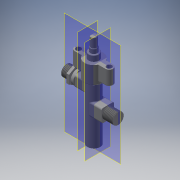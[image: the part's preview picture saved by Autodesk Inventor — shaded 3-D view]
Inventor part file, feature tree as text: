
AUTODESK INVENTOR PART (.ipt)
format: ipt  version: 2018 (Build 220112000, 112)  size: 577,024 bytes
history: native  units: mm
features: extrude x15, sketch x15, fillet x6, projected_geometry x5, hole x3, plane x3, thread x2
ambient origin geometry x8: Origin, YZ Plane, XZ Plane, XY Plane, X Axis, Y Axis, Z Axis, Center Point
bodies: Volumenkörper1 (feature_tree)
feature tree (49):
  extrude  "Extrusion1"  Depth=18.0mm
  extrude  "Extrusion2"  Depth=10.675mm
  extrude  "Extrusion3"  Depth=17.0mm TaperAngle=0.0deg
  extrude  "Extrusion4"  Depth=6.5mm TaperAngle=0.0deg
  hole  "Bohrung1"  [1 undecoded]
  hole  "Bohrung2"  [1 undecoded]
  extrude  "Extrusion5"  Depth=10.0mm
  extrude  "Extrusion6"  Depth=10.0mm
  plane  "Arbeitsebene1"
  extrude  "Extrusion7"  Depth=8.0mm TaperAngle=0.0deg
  extrude  "Extrusion8"  Depth=66.0mm TaperAngle=0.0deg
  thread  "Gewinde1"  [1 undecoded]
  extrude  "Extrusion9"  Depth=19.0mm
  plane  "Arbeitsebene2"
  extrude  "Extrusion10"  Depth=13.0mm
  extrude  "Extrusion11"  Depth=10.0mm TaperAngle=0.0deg
  fillet  "Rundung1"  Radius=6.0mm
  fillet  "Rundung2"  Radius=13.0mm
  extrude  "Extrusion12"  Depth=5.0mm
  fillet  "Rundung3"  Radius=8.8mm
  fillet  "Rundung4"  Radius=16.0mm
  fillet  "Rundung5"  Radius=3.0mm
  fillet  "Rundung6"  Radius=2.0mm
  extrude  "Extrusion13"  Depth=6.0mm TaperAngle=0.0deg
  extrude  "Extrusion14"  Depth=8.0mm
  extrude  "Extrusion15"  Depth=8.0mm
  thread  "Gewinde2"  [1 undecoded]
  hole  "Bohrung4"  [1 undecoded]
  plane  "Arbeitsebene3"
  sketch  "Skizze1"  dims[d0=21.35mm d1=18.0mm]
  sketch  "Skizze2"  dims[d2=9.0mm d3=10.675mm]
  sketch  "Skizze3"  dims[d4=10.675mm d5=17.0mm d6=0.0mm]
  sketch  "Skizze4"  dims[d7=12.0mm d8=6.5mm d9=0.0mm]
  sketch  "Skizze5"  dims[d10=8.0mm d11=5.5mm d12=0.0mm]
  sketch  "Skizze6"  dims[d13=7.0mm d14=10.6mm d15=0.0mm]
  sketch  "Skizze7"  dims[d16=2.0mm d17=10.0mm d18=10.0mm]
  projected_geometry  "Projizierte Kontur1"
  projected_geometry  "Projizierte Kontur2"
  sketch  "Skizze8"  dims[d19=6.0mm d20=6.0mm d21=4.0mm d22=2.0mm d23=90.0deg d24=8.0mm d25=20.594885mm d26=10.0mm d27=10.0mm]
  sketch  "Skizze10"  dims[d28=6.0mm d29=6.0mm d30=4.0mm d31=2.0mm d32=90.0deg d33=8.0mm d34=20.594885mm d35=3.8mm d36=0.0mm]
  projected_geometry  "Projizierte Kontur3"
  sketch  "Skizze11"  dims[d37=14.75mm d38=66.0mm d39=0.0mm d40=14.5mm]
  sketch  "Skizze12"  dims[d41=15.4mm d43=19.0mm]
  sketch  "Skizze13"  dims[d44=9.0mm d45=0.0mm d46=13.0mm]
  projected_geometry  "Projizierte Kontur4"
  projected_geometry  "Projizierte Kontur5"
  sketch  "Skizze14"  dims[d47=12.0mm d48=0.0mm d49=10.0mm d50=0.0mm d60=6.0mm d61=0.0mm d62=13.0mm]
  sketch  "Skizze15"  dims[d63=13.0mm d64=5.0mm d65=8.8mm d66=0.0mm d67=16.0mm d68=3.0mm d69=0.0mm d70=2.0mm]
  sketch  "Skizze16"  dims[d71=1.0mm d72=6.0mm d73=0.0mm d74=1.0mm d75=1.0mm d76=0.5mm d77=0.5mm d78=10.0mm d79=1.5mm d80=0.0mm d81=17.0mm d82=3.0mm d83=0.0mm d84=13.0mm d85=8.0mm d86=0.0mm d87=10.0mm d88=0.0mm d89=10.0mm d90=10.0mm d91=10.0mm d92=6.0mm d93=12.0mm d94=2.0mm d95=90.0deg d96=8.0mm d97=20.594885mm]
note: 5 required parameter values undecoded (feature->parameter linkage not recoverable at this tier; creation-order binding heuristic only, values carry confidence <= 0.55)
